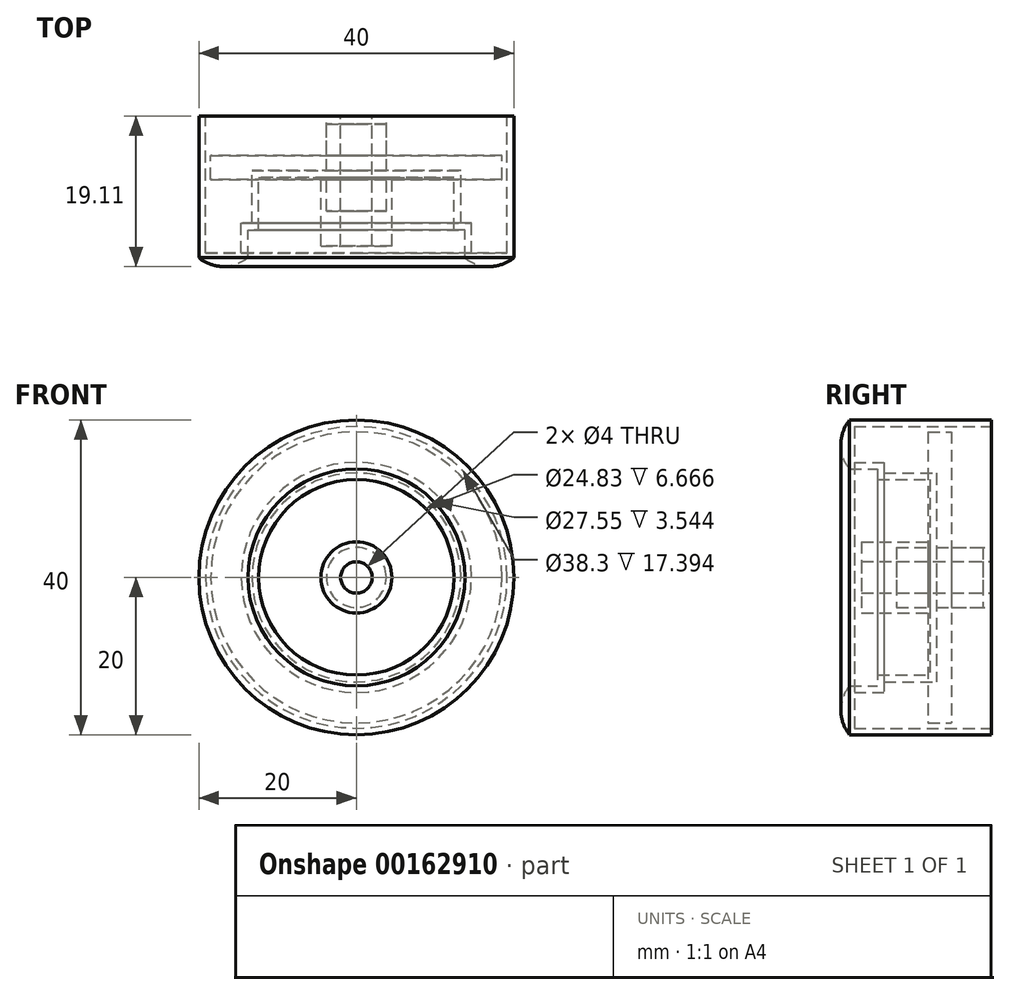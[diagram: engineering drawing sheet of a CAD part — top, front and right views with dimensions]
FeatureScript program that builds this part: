
annotation { "Feature Type Name" : "Feature", "Feature Type Description" : "" }
export const myFeature = defineFeature(function(context is Context, id is Id, definition is map)
    precondition{}
    {
        {
            var Q0;
            Q0=qCreatedBy(makeId("Top.planeOp"),FACE);
            var sketch = newSketch(context, id + "F0", { "sketchPlane" : qUnion([Q0])});
            skLineSegment(sketch, "E0", {"start": v(0, 17.4) * mm, "end": v(0, -20.43) * mm, "construction": true});
            skLineSegment(sketch, "E1", {"start": v(2, 6.54) * mm, "end": v(2, -9.96) * mm});
            skLineSegment(sketch, "E2", {"start": v(2, -9.96) * mm, "end": v(4.51, -9.96) * mm});
            skLineSegment(sketch, "E3", {"start": v(4.51, -9.96) * mm, "end": v(4.51, -1.25) * mm});
            skLineSegment(sketch, "E4", {"start": v(4.51, -1.25) * mm, "end": v(12.42, -1.25) * mm});
            skLineSegment(sketch, "E5", {"start": v(12.42, -1.25) * mm, "end": v(12.42, -7.92) * mm});
            skLineSegment(sketch, "E6", {"start": v(12.42, -7.92) * mm, "end": v(13.78, -7.92) * mm});
            skLineSegment(sketch, "E7", {"start": v(13.78, -7.92) * mm, "end": v(13.78, -11.46) * mm});
            skLineSegment(sketch, "E8", {"start": v(20, -11.46) * mm, "end": v(20, 6.54) * mm});
            skLineSegment(sketch, "E9.0", {"start": v(19.15, -10.86) * mm, "end": v(19.15, 6.54) * mm});
            skLineSegment(sketch, "E9.1", {"start": v(14.62, -10.86) * mm, "end": v(19.15, -10.86) * mm});
            skLineSegment(sketch, "E9.2", {"start": v(14.62, -7.07) * mm, "end": v(14.62, -10.86) * mm});
            skLineSegment(sketch, "E9.3", {"start": v(13.27, -7.07) * mm, "end": v(14.62, -7.07) * mm});
            skLineSegment(sketch, "E9.4", {"start": v(13.27, -0.4) * mm, "end": v(13.27, -7.07) * mm});
            skLineSegment(sketch, "E9.8", {"start": v(3.8, -0.4) * mm, "end": v(13.27, -0.4) * mm});
            skLineSegment(sketch, "E10", {"start": v(19.15, 6.54) * mm, "end": v(20, 6.54) * mm});
            skLineSegment(sketch, "E11", {"start": v(2, 6.54) * mm, "end": v(3.8, 6.54) * mm});
            skLineSegment(sketch, "E12", {"start": v(3.8, 6.54) * mm, "end": v(3.8, -0.4) * mm});
            skArc(sketch, "E13", {"start": v(13.78, -11.46) * mm, "mid": v(16.89, -12.57) * mm, "end": v(20, -11.46) * mm});
            skLineSegment(sketch, "E14", {"start": v(16.89, -10.86) * mm, "end": v(16.89, -7.65) * mm, "construction": true});
            skSolve(sketch);
        }
        {
            var Q0;
            Q0=makeQuery(id+"F0.imprint","IMPRINT",FACE,{"disambiguationData":[TD([[makeQuery(id+"F0.imprint","IMPRINT",EDGE,{"derivedFrom":sQuery(id+"F0.wireOp",EDGE,"E1")}),1.0]])]});
            var Q1;
            Q1=sQuery(id+"F0.wireOp",EDGE,"E0");
            revolve(context, id + "F1", {"entities" : qUnion([Q0]), "axis" : qUnion([Q1]), "revolveType" : RevolveType.FULL});
        }
        {
            var Q0;
            Q0=qCreatedBy(makeId("Top.planeOp"),FACE);
            var sketch = newSketch(context, id + "F2", { "sketchPlane" : qUnion([Q0])});
            skLineSegment(sketch, "E15.0", {"start": v(0, 17.4) * mm, "end": v(0, -20.43) * mm, "construction": true});
            skLineSegment(sketch, "E16.0", {"start": v(2, 5.5) * mm, "end": v(2, -5.5) * mm});
            skLineSegment(sketch, "E17", {"start": v(3.8, 5.5) * mm, "end": v(3.8, 1.5) * mm});
            skLineSegment(sketch, "E18", {"start": v(3.8, 1.5) * mm, "end": v(18.5, 1.5) * mm});
            skLineSegment(sketch, "E19", {"start": v(18.5, 1.5) * mm, "end": v(18.5, -1.5) * mm});
            skLineSegment(sketch, "E20", {"start": v(18.5, -1.5) * mm, "end": v(3.8, -1.5) * mm});
            skLineSegment(sketch, "E21", {"start": v(3.8, -1.5) * mm, "end": v(3.8, -5.5) * mm});
            skLineSegment(sketch, "E22", {"start": v(2, -5.5) * mm, "end": v(3.8, -5.5) * mm});
            skLineSegment(sketch, "E23", {"start": v(0, 0) * mm, "end": v(6.69, 0) * mm, "construction": true});
            skLineSegment(sketch, "E24", {"start": v(2, 5.5) * mm, "end": v(3.8, 5.5) * mm});
            skSolve(sketch);
        }
        {
            var Q0;
            Q0 = qSketchRegion(id + "F2", true);
            var Q1;
            Q1=sQuery(id+"F2.wireOp",EDGE,"E15.0");
            revolve(context, id + "F3", {"entities" : qUnion([Q0]), "axis" : qUnion([Q1]), "revolveType" : RevolveType.FULL});
        }
    });
